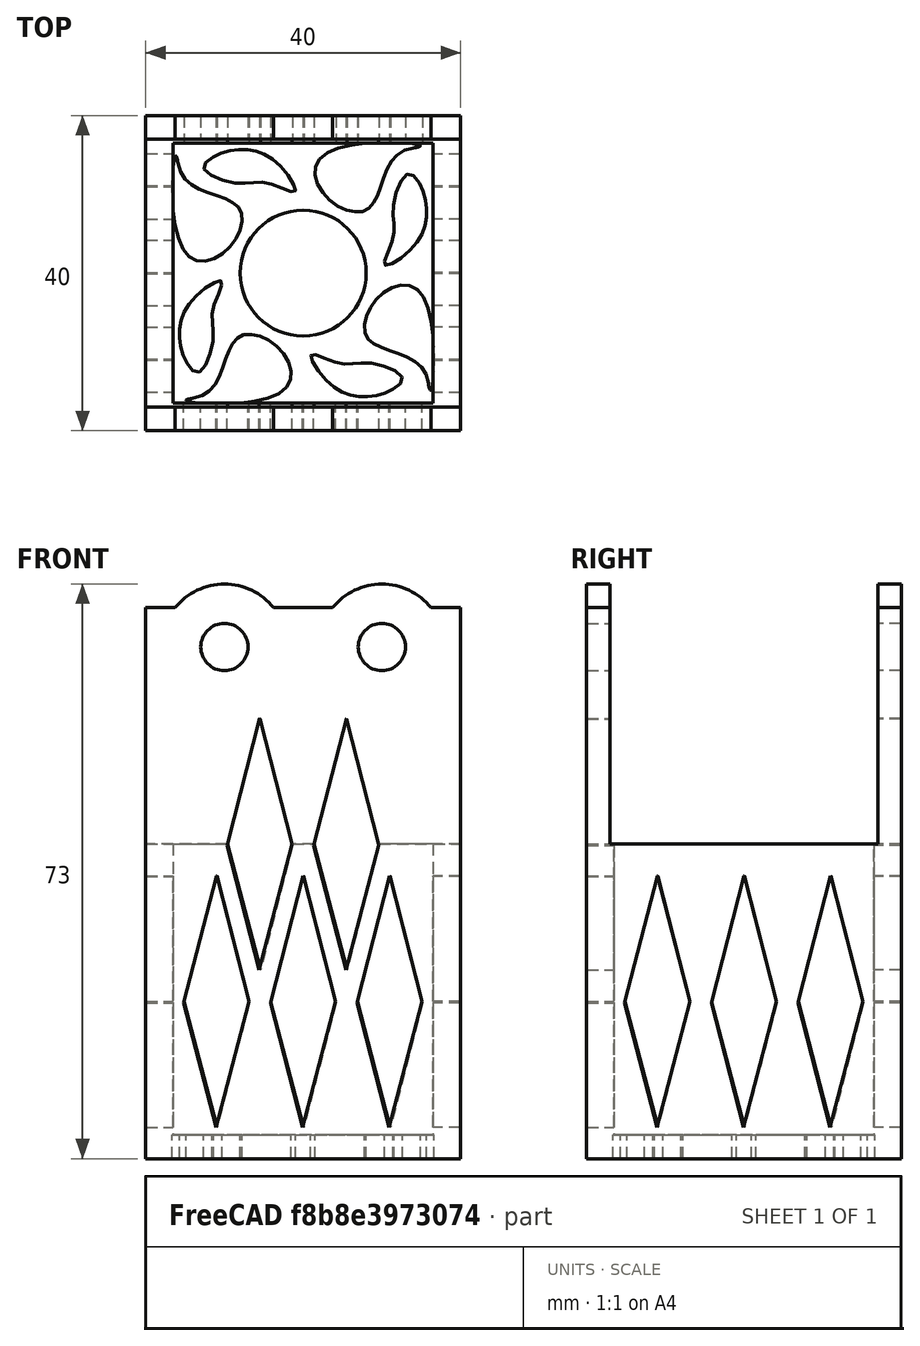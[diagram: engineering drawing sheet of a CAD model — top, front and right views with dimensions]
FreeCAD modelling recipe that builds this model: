
FCSTD DOCUMENT  (FreeCAD 0.16R6700 (Git))
Label: Laser mount v 2
License: All rights reserved
LicenseURL: http://en.wikipedia.org/wiki/All_rights_reserved
objects: Part::Part2DObjectPython×8, Part::Extrusion×8, Part::MultiFuse×6, Part::Cut×6, Part::FeaturePython×5, Part::Cylinder×5, Part::Box×2
note: 40 computed .brp shape members not serialized (recipe doc carries the construction recipe); baked Part::Feature solids carry a one-line shape summary decoded from their .brp

FEATURE [Part::Part2DObjectPython] DWire003  # Draft 2D object (typed FeaturePython)
  ChamferSize = 0
  Closed = true
  End = (0.0399391,-20,35.8827)
  FilletRadius = 0
  Length = 66.0594
  MakeFace = true
  Points = (5) [(-0.0217852,-20,35.9444),(-4.15705,-20,19.7737),(-0.0835034,-20,3.97325),(4.11348,-20,19.9588),(0.0399391,-20,35.8827)]
  Start = (-0.0217852,-20,35.9444)
  Subdivisions = 0
FEATURE [Part::Part2DObjectPython] DWire004  # Draft 2D object (typed FeaturePython)
  ChamferSize = 0
  Closed = true
  End = (-10.9601,-20,35.8827)
  FilletRadius = 0
  Length = 66.0594
  MakeFace = true
  Placement = pos=(-11,0,0) rot=(0,0,1;0rad)
  Points = (5) [(-0.0217852,-20,35.9444),(-4.15705,-20,19.7737),(-0.0835034,-20,3.97325),(4.11348,-20,19.9588),(0.0399391,-20,35.8827)]
  Start = (-11.0218,-20,35.9444)
  Subdivisions = 0
FEATURE [Part::Part2DObjectPython] DWire005  # Draft 2D object (typed FeaturePython)
  ChamferSize = 0
  Closed = true
  End = (11.0399,-20,35.8827)
  FilletRadius = 0
  Length = 66.0594
  MakeFace = true
  Placement = pos=(11,0,0) rot=(0,0,1;0rad)
  Points = (5) [(-0.0217852,-20,35.9444),(-4.15705,-20,19.7737),(-0.0835034,-20,3.97325),(4.11348,-20,19.9588),(0.0399391,-20,35.8827)]
  Start = (10.9782,-20,35.9444)
  Subdivisions = 0
FEATURE [Part::Extrusion] Extrude006
  Base = -> DWire003
  Dir = (0,3.5,0)
  Solid = false
FEATURE [Part::Extrusion] Extrude007
  Base = -> DWire004
  Dir = (0,3.5,0)
  Solid = false
FEATURE [Part::Extrusion] Extrude008
  Base = -> DWire005
  Dir = (0,3.5,0)
  Solid = false
FEATURE [Part::MultiFuse] Fusion002  label="Side Vents001"
  Shapes = -> [Extrude006,Extrude007,Extrude008]
FEATURE [Part::FeaturePython] Array002  label="Polar array of side vents"  # Draft array (typed FeaturePython)
  Angle = 360
  ArrayType = 1
  Axis = (0,0,1)
  Base = -> Fusion002
  Center = (0,0,0)
  Fuse = false
  IntervalAxis = (0,0,0)
  IntervalX = (1,0,0)
  IntervalY = (0,1,0)
  IntervalZ = (0,0,0)
  NumberPolar = 4
  NumberX = 2
  NumberY = 2
  NumberZ = 1
FEATURE [Part::Box] Box001  label="Cube001"
  Height = 30
  Length = 40
  Placement = pos=(-20,17,40) rot=(0,0,1;0rad)
  Width = 3
FEATURE [Part::Cylinder] Cylinder001
  Angle = 360
  Height = 3
  Placement = pos=(-10,20,65) rot=(1,0,0;1.5708rad)
  Radius = 3
FEATURE [Part::Cylinder] Cylinder002
  Angle = 360
  Height = 3
  Placement = pos=(-10,20,65) rot=(1,0,0;1.5708rad)
  Radius = 8
FEATURE [Part::Cylinder] Cylinder003
  Angle = 360
  Height = 3
  Placement = pos=(10,20,65) rot=(1,0,0;1.5708rad)
  Radius = 3
FEATURE [Part::Cylinder] Cylinder004
  Angle = 360
  Height = 3
  Placement = pos=(10,20,65) rot=(1,0,0;1.5708rad)
  Radius = 8
FEATURE [Part::MultiFuse] Fusion003  label="Screw point Left"
  Shapes = -> [Cylinder002,Box001,Cylinder004]
FEATURE [Part::MultiFuse] Fusion004  label="Screw holes"
  Shapes = -> [Cylinder003,Cylinder001]
FEATURE [Part::Cut] Cut005  label="Screw mounting point"
  Base = -> Fusion003
  Tool = -> Fusion004
FEATURE [Part::FeaturePython] Array003  label="Screw mounting points"  # Draft array (typed FeaturePython)
  Angle = 360
  ArrayType = 1
  Axis = (0,0,1)
  Base = -> Cut005
  Center = (0,0,0)
  Fuse = false
  IntervalAxis = (0,0,0)
  IntervalX = (1,0,0)
  IntervalY = (0,1,0)
  IntervalZ = (0,0,0)
  NumberPolar = 2
  NumberX = 2
  NumberY = 2
  NumberZ = 1
FEATURE [Part::Box] Box002  label="Cube002"
  Height = 40
  Length = 40
  Placement = pos=(-20,-20,0) rot=(0,0,1;0rad)
  Width = 40
FEATURE [Part::Part2DObjectPython] Rectangle001  # Draft 2D object (typed FeaturePython)
  ChamferSize = 0
  Columns = 1
  FilletRadius = 0
  Height = 33
  Length = 33
  MakeFace = true
  Placement = pos=(16.5,16.5,40) rot=(0,0,1;3.14159rad)
  Rows = 1
FEATURE [Part::Extrusion] Extrude009
  Base = -> Rectangle001
  Dir = (0,0,-37)
  Solid = false
FEATURE [Part::Cut] Cut007
  Base = -> Box002
  Tool = -> Extrude009
FEATURE [Part::Cylinder] Cylinder005
  Angle = 360
  Height = 3
  Radius = 8
FEATURE [Part::Cut] Cut008  label="Chassis001"
  Base = -> Cut007
  Tool = -> Cylinder005
FEATURE [Part::Part2DObjectPython] BSpline003  label="Base vents 003"  # Draft 2D object (typed FeaturePython)
  Closed = true
  MakeFace = true
  Points = (5) [(-13.967,-15.8985,0),(-11.0044,-13.8617,0),(-8,-8,0),(-2.79563,-9.84993,0),(-2.11671,-14.5407,0)]
FEATURE [Part::FeaturePython] Array005  label="Base Vents 002"  # Draft array (typed FeaturePython)
  Angle = 360
  ArrayType = 1
  Axis = (0,0,1)
  Base = -> BSpline003
  Center = (0,0,0)
  Fuse = false
  IntervalAxis = (0,0,0)
  IntervalX = (1,0,0)
  IntervalY = (0,1,0)
  IntervalZ = (0,0,0)
  NumberPolar = 4
  NumberX = 2
  NumberY = 2
  NumberZ = 1
FEATURE [Part::Part2DObjectPython] BSpline004  # Draft 2D object (typed FeaturePython)
  Closed = true
  MakeFace = true
  Points = (6) [(-14.0287,-12.3805,-1.52656e-16),(-15.6335,-8.73896,0),(-13.2264,-2.56692,0),(-10.3872,-1.02391,0),(-11.4365,-4.48025,0),(-11.4365,-8.49208,0)]
FEATURE [Part::FeaturePython] Array006  label="Base vents 004"  # Draft array (typed FeaturePython)
  Angle = 360
  ArrayType = 1
  Axis = (0,0,1)
  Base = -> BSpline004
  Center = (0,0,0)
  Fuse = false
  IntervalAxis = (0,0,0)
  IntervalX = (1,0,0)
  IntervalY = (0,1,0)
  IntervalZ = (0,0,0)
  NumberPolar = 4
  NumberX = 2
  NumberY = 2
  NumberZ = 1
FEATURE [Part::Extrusion] Extrude010
  Base = -> Array005
  Dir = (0,0,3)
  Solid = false
FEATURE [Part::Extrusion] Extrude011
  Base = -> Array006
  Dir = (0,0,3)
  Solid = false
FEATURE [Part::MultiFuse] Fusion006  label="Base vents001"
  Shapes = -> [Extrude010,Extrude011]
FEATURE [Part::Cut] Cut009  label="Chassis with base vents001"
  Base = -> Cut008
  Tool = -> Fusion006
FEATURE [Part::Cut] Cut010  label="Chassis with all vents (thicker)"
  Base = -> Cut009
  Tool = -> Array002
FEATURE [Part::MultiFuse] Fusion007  label="Mount without upper vents (thicker)"
  Shapes = -> [Cut010,Array003]
FEATURE [Part::Part2DObjectPython] DWire006  # Draft 2D object (typed FeaturePython)
  ChamferSize = 0
  Closed = true
  End = (0.0399391,-20,35.8827)
  FilletRadius = 0
  Length = 66.0594
  MakeFace = true
  Points = (5) [(-0.0217852,-20,35.9444),(-4.15705,-20,19.7737),(-0.0835034,-20,3.97325),(4.11348,-20,19.9588),(0.0399391,-20,35.8827)]
  Start = (-0.0217852,-20,35.9444)
  Subdivisions = 0
FEATURE [Part::Extrusion] Extrude012
  Base = -> DWire006
  Dir = (0,3.5,0)
  Placement = pos=(-5.5,0,20) rot=(0,0,1;0rad)
  Solid = false
FEATURE [Part::Part2DObjectPython] DWire007  # Draft 2D object (typed FeaturePython)
  ChamferSize = 0
  Closed = true
  End = (0.0399391,-20,35.8827)
  FilletRadius = 0
  Length = 66.0594
  MakeFace = true
  Points = (5) [(-0.0217852,-20,35.9444),(-4.15705,-20,19.7737),(-0.0835034,-20,3.97325),(4.11348,-20,19.9588),(0.0399391,-20,35.8827)]
  Start = (-0.0217852,-20,35.9444)
  Subdivisions = 0
FEATURE [Part::Extrusion] Extrude013
  Base = -> DWire007
  Dir = (0,3.5,0)
  Placement = pos=(5.5,0,20) rot=(0,0,1;0rad)
  Solid = false
FEATURE [Part::MultiFuse] Fusion008  label="Upper vents (thicker)"
  Shapes = -> [Extrude012,Extrude013]
FEATURE [Part::FeaturePython] Array007  # Draft array (typed FeaturePython)
  Angle = 360
  ArrayType = 1
  Axis = (0,0,1)
  Base = -> Fusion008
  Center = (0,0,0)
  Fuse = false
  IntervalAxis = (0,0,0)
  IntervalX = (1,0,0)
  IntervalY = (0,1,0)
  IntervalZ = (0,0,0)
  NumberPolar = 2
  NumberX = 2
  NumberY = 2
  NumberZ = 1
FEATURE [Part::Cut] Cut011  label="Complete laser mount 002"
  Base = -> Fusion007
  Tool = -> Array007
